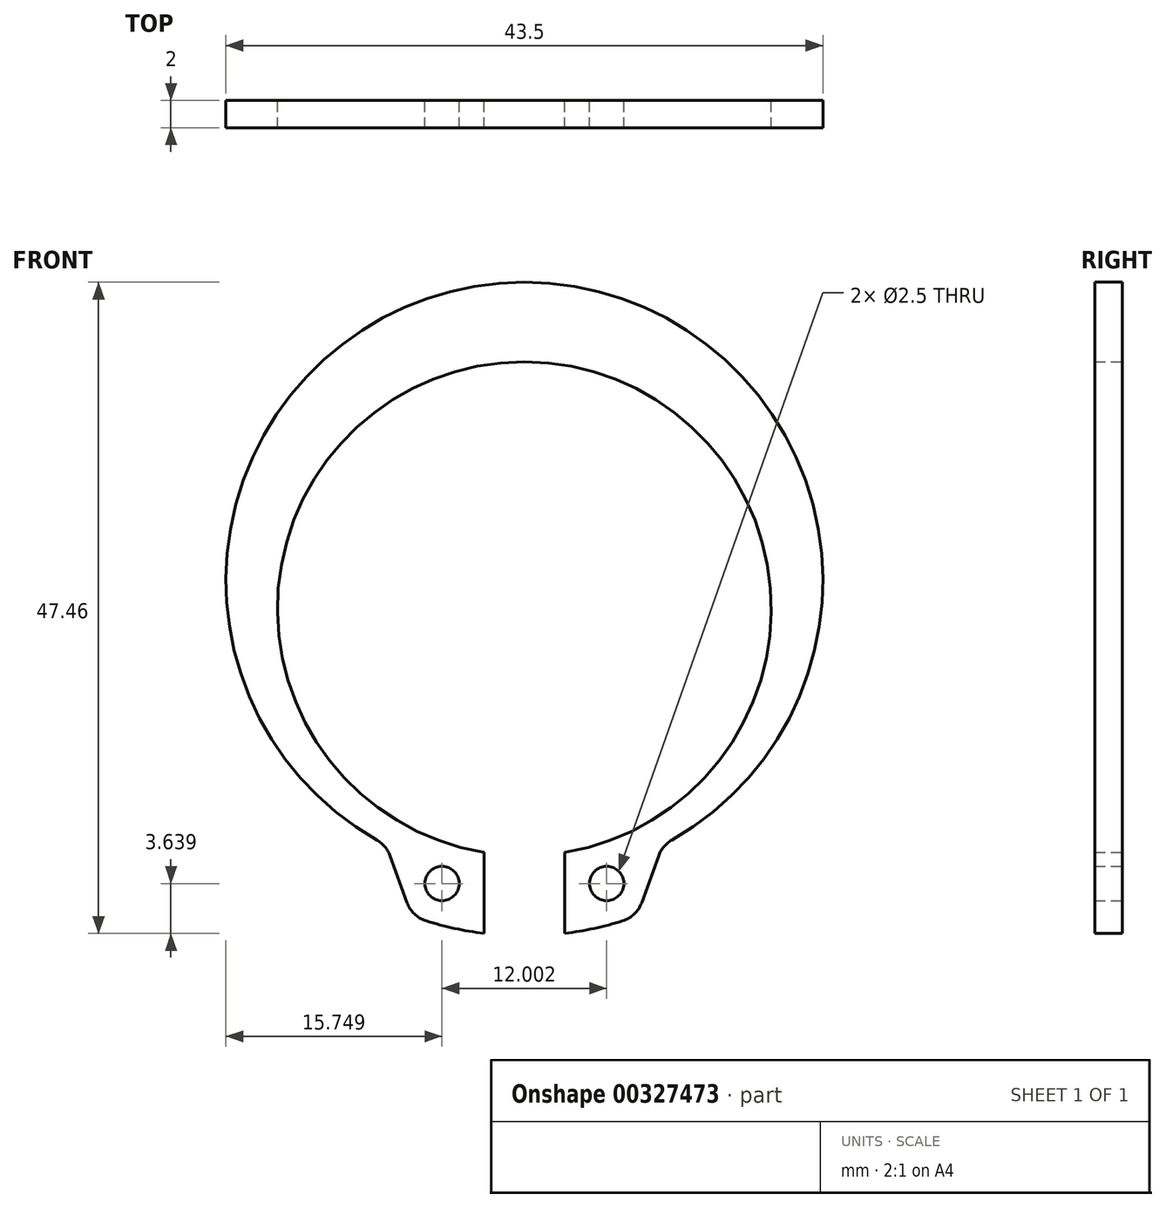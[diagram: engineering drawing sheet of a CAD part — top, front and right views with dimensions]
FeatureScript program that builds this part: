
annotation { "Feature Type Name" : "Feature", "Feature Type Description" : "" }
export const myFeature = defineFeature(function(context is Context, id is Id, definition is map)
    precondition{}
    {
        {
            var Q0;
            Q0=qCreatedBy(makeId("Front.planeOp"),FACE);
            var sketch = newSketch(context, id + "F0", { "sketchPlane" : qUnion([Q0])});
            skCircle(sketch, "E0", {"center": v(0, 0) * mm, "radius": 25.5 * mm, "construction": true});
            skLineSegment(sketch, "E1", {"start": v(0, 0) * mm, "end": v(0, 19.5) * mm, "construction": true});
            skLineSegment(sketch, "E2", {"start": v(0, 0) * mm, "end": v(-25.5, 0) * mm, "construction": true});
            skLineSegment(sketch, "E3", {"start": v(0, 0) * mm, "end": v(25.5, 0) * mm, "construction": true});
            skLineSegment(sketch, "E4", {"start": v(0, 0) * mm, "end": v(0, -25.5) * mm, "construction": true});
            skCircle(sketch, "E5", {"center": v(0, 0) * mm, "radius": 19.5 * mm, "construction": true});
            skArc(sketch, "E6", {"start": v(2.95, -17.76) * mm, "mid": v(0, 18) * mm, "end": v(-2.95, -17.76) * mm});
            skLineSegment(sketch, "E7", {"start": v(0, -17.76) * mm, "end": v(-2.95, -17.76) * mm, "construction": true});
            skLineSegment(sketch, "E8", {"start": v(0, -17.76) * mm, "end": v(2.95, -17.76) * mm, "construction": true});
            skLineSegment(sketch, "E9", {"start": v(2.95, -17.76) * mm, "end": v(2.95, -23.66) * mm});
            skLineSegment(sketch, "E10", {"start": v(-2.95, -17.76) * mm, "end": v(-2.95, -23.66) * mm});
            skCircle(sketch, "E11", {"center": v(-6, -20.02) * mm, "radius": 1.25 * mm});
            skPoint(sketch, "E12", {"position": v(0, -19.7) * mm});
            skArc(sketch, "E13", {"start": v(2.95, -19.5) * mm, "mid": v(0, 23.8) * mm, "end": v(-2.95, -19.5) * mm});
            skLineSegment(sketch, "E14", {"start": v(0, 19.5) * mm, "end": v(0, 23.8) * mm, "construction": true});
            skLineSegment(sketch, "E15", {"start": v(0, 23.8) * mm, "end": v(0, 25.5) * mm, "construction": true});
            skLineSegment(sketch, "E16", {"start": v(-6, -20.02) * mm, "end": v(-2.95, -20.02) * mm, "construction": true});
            skLineSegment(sketch, "E17", {"start": v(-6, -20.02) * mm, "end": v(-6, -16.97) * mm, "construction": true});
            skArc(sketch, "E18", {"start": v(0, -23.84) * mm, "mid": v(4.16, -23.47) * mm, "end": v(8.2, -22.39) * mm});
            skLineSegment(sketch, "E19", {"start": v(-6, -20.02) * mm, "end": v(-6, -23.07) * mm, "construction": true});
            skLineSegment(sketch, "E20", {"start": v(-6, -20.02) * mm, "end": v(-9.05, -20.02) * mm, "construction": true});
            skLineSegment(sketch, "E21", {"start": v(-8.2, -22.39) * mm, "end": v(-10.07, -17.23) * mm});
            skLineSegment(sketch, "E22.MirrorCS", {"start": v(6, -20.02) * mm, "end": v(2.95, -20.02) * mm, "construction": true});
            skLineSegment(sketch, "E23.MirrorCS", {"start": v(6, -20.02) * mm, "end": v(6, -23.07) * mm, "construction": true});
            skCircle(sketch, "E24.MirrorC", {"center": v(6, -20.02) * mm, "radius": 1.25 * mm});
            skLineSegment(sketch, "E25.MirrorCS", {"start": v(6, -20.02) * mm, "end": v(9.05, -20.02) * mm, "construction": true});
            skLineSegment(sketch, "E26.MirrorCS", {"start": v(6, -20.02) * mm, "end": v(6, -16.97) * mm, "construction": true});
            skLineSegment(sketch, "E27.MirrorCS", {"start": v(8.2, -22.39) * mm, "end": v(10.07, -17.23) * mm});
            skArc(sketch, "E28.trimOffspring", {"start": v(-8.2, -22.39) * mm, "mid": v(-5.6, -23.17) * mm, "end": v(-2.95, -23.66) * mm});
            skSolve(sketch);
        }
        {
            var Q0;
            Q0=qSketchRegion(id+"F0",true);
            extrude(context, id + "F1", {"entities" : qUnion([Q0]), "depth" : 2 * mm});
        }
        {
            var Q0;
            Q0=makeQuery(id+"F1.opExtrude","SWEPT_EDGE",EDGE,{"disambiguationData":[OSD([sQuery(id+"F0.wireOp",EDGE,"907c1e65-be0d-4d4d-923e-d7fc0afcae600.MirrorCS"),sQuery(id+"F0.wireOp",EDGE,"ea3ce9a1-426e-48f8-a769-742e162fd32d0.MirrorCS")])]});
            var Q1;
            Q1=makeQuery(id+"F1.opExtrude","SWEPT_EDGE",EDGE,{"disambiguationData":[OSD([sQuery(id+"F0.wireOp",EDGE,"yB3Dk9i2-sZMU-oLhI-pwqJ-xhCv1nncbOm0"),sQuery(id+"F0.wireOp",EDGE,"pRWJiajO-2Cuv-CeR1-zJug-2Vsa7C0coXul")])]});
            var Q2;
            Q2=makeQuery(id+"F1.opExtrude","SWEPT_EDGE",EDGE,{"disambiguationData":[OSD([sQuery(id+"F0.wireOp",EDGE,"E13"),sQuery(id+"F0.wireOp",EDGE,"E21")])]});
            var Q3;
            Q3=makeQuery(id+"F1.opExtrude","SWEPT_EDGE",EDGE,{"disambiguationData":[OSD([sQuery(id+"F0.wireOp",EDGE,"E21"),sQuery(id+"F0.wireOp",EDGE,"E28.trimOffspring")])]});
            var Q4;
            Q4=makeQuery(id+"F1.opExtrude","SWEPT_EDGE",EDGE,{"disambiguationData":[OSD([sQuery(id+"F0.wireOp",EDGE,"E18"),sQuery(id+"F0.wireOp",EDGE,"E27.MirrorCS")])]});
            var Q5;
            Q5=makeQuery(id+"F1.opExtrude","SWEPT_EDGE",EDGE,{"disambiguationData":[OSD([sQuery(id+"F0.wireOp",EDGE,"E13"),sQuery(id+"F0.wireOp",EDGE,"E27.MirrorCS")])]});
            fillet(context, id + "F2", {"entities" : qUnion([Q0, Q1, Q2, Q3, Q4, Q5]), "radius" : 2.15 * mm, "tangentPropagation" : true, "allowEdgeOverflow" : false});
        }
    });
